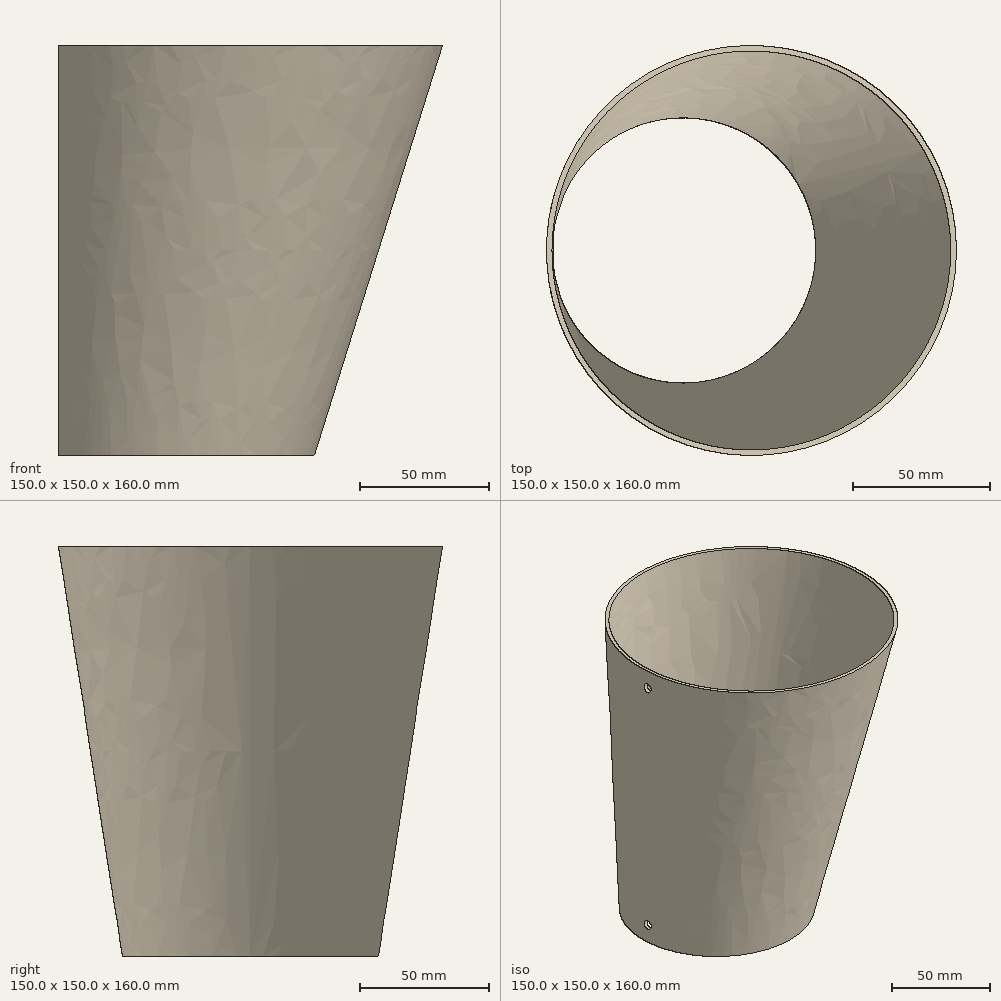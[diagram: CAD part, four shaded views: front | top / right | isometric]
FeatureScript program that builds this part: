
annotation { "Feature Type Name" : "Feature", "Feature Type Description" : "" }
export const myFeature = defineFeature(function(context is Context, id is Id, definition is map)
    precondition{}
    {
        {
            var Q0;
            Q0=qCreatedBy(makeId("Top.planeOp"),FACE);
            var sketch = newSketch(context, id + "F0", { "sketchPlane" : qUnion([Q0])});
            skCircle(sketch, "E0", {"center": v(50, 0) * mm, "radius": 50 * mm});
            skSolve(sketch);
        }
        {
            var Q0;
            Q0=qCreatedBy(makeId("Top.planeOp"),FACE);
            cPlane(context, id + "F1", {"entities" : qUnion([Q0]), "cplaneType" : CPlaneType.OFFSET, "offset" : 160 * mm, "width" : 150 * mm, "height" : 150 * mm});
        }
        {
            var Q0;
            Q0=qCreatedBy(id+"F1.planeOp",FACE);
            var sketch = newSketch(context, id + "F2", { "sketchPlane" : qUnion([Q0])});
            skCircle(sketch, "E1", {"center": v(75, 0) * mm, "radius": 75 * mm});
            skSolve(sketch);
        }
        {
            var Q0;
            Q0=makeQuery(id+"F2.imprint","IMPRINT",FACE,{"disambiguationData":[TD([[makeQuery(id+"F2.imprint","IMPRINT",EDGE,{"derivedFrom":sQuery(id+"F2.wireOp",EDGE,"E1")}),1.0]])]});
            var Q1;
            Q1=makeQuery(id+"F0.imprint","IMPRINT",FACE,{"disambiguationData":[TD([[makeQuery(id+"F0.imprint","IMPRINT",EDGE,{"derivedFrom":sQuery(id+"F0.wireOp",EDGE,"E0")}),1.0]])]});
            loft(context, id + "F3", {"sheetProfilesArray" : [{ "sheetProfileEntities" : qUnion([Q0]) }, { "sheetProfileEntities" : qUnion([Q1]) }]});
        }
        {
            var Q0;
            Q0=makeQuery(id+"F3.opLoft","CAP_FACE",FACE,{"disambiguationData":[OSD([makeQuery(id+"F2.imprint","IMPRINT",FACE,{"disambiguationData":[TD([[makeQuery(id+"F2.imprint","IMPRINT",EDGE,{"derivedFrom":sQuery(id+"F2.wireOp",EDGE,"E1")}),1.0]])]})])],"isStart":true});
            shell(context, id + "F4", {"entities" : qUnion([Q0]), "thickness" : 2 * mm});
        }
        {
            var Q0;
            Q0=qCreatedBy(makeId("Right.planeOp"),FACE);
            var sketch = newSketch(context, id + "F5", { "sketchPlane" : qUnion([Q0])});
            skCircle(sketch, "E2", {"center": v(0, 150) * mm, "radius": 2.5 * mm});
            skCircle(sketch, "E3", {"center": v(0, 10) * mm, "radius": 2.5 * mm});
            skSolve(sketch);
        }
        {
            var Q0;
            Q0 = qSketchRegion(id + "F5", true);
            extrude(context, id + "F6", {"entities" : qUnion([Q0]), "operationType" : NewBodyOperationType.REMOVE, "endBound" : BoundingType.UP_TO_NEXT, "depth" : 25 * mm});
        }
        {
            var Q0;
            Q0=makeQuery(id+"F3.opLoft","CAP_FACE",FACE,{"disambiguationData":[OSD([makeQuery(id+"F0.imprint","IMPRINT",FACE,{"disambiguationData":[TD([[makeQuery(id+"F0.imprint","IMPRINT",EDGE,{"derivedFrom":sQuery(id+"F0.wireOp",EDGE,"E0")}),1.0]])]})])],"isStart":true});
            var sketch = newSketch(context, id + "F7", { "sketchPlane" : qUnion([Q0])});
            skCircle(sketch, "E4", {"center": v(50, 0) * mm, "radius": 47.95 * mm});
            skSolve(sketch);
        }
        {
            var Q0;
            Q0=sQuery(id+"F7.wireOp",VERTEX,"E4.center");
            var Q1;
            Q1=makeQuery(id+"F3.opLoft","SWEPT_BODY",BODY,{"disambiguationData":[OSD([makeQuery(id+"F0.imprint","IMPRINT",FACE,{"disambiguationData":[TD([[makeQuery(id+"F0.imprint","IMPRINT",EDGE,{"derivedFrom":sQuery(id+"F0.wireOp",EDGE,"E0")}),1.0]])]}),makeQuery(id+"F2.imprint","IMPRINT",FACE,{"disambiguationData":[TD([[makeQuery(id+"F2.imprint","IMPRINT",EDGE,{"derivedFrom":sQuery(id+"F2.wireOp",EDGE,"E1")}),1.0]])]})])]});
            hole(context, id + "F8", {"style" : HoleStyle.C_BORE, "endStyle" : HoleEndStyle.THROUGH, "holeDiameter" : 15 * mm, "cBoreDiameter" : 97 * mm, "cBoreDepth" : 5 * mm, "isTappedThrough" : true, "tappedDepth" : 12 * mm, "tapClearance" : 3, "locations" : qUnion([Q0]), "scope" : qUnion([Q1])});
        }
    });
